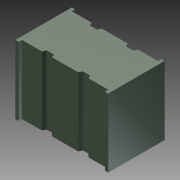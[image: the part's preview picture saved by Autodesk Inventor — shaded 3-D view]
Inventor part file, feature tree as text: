
AUTODESK INVENTOR PART (.ipt)
format: ipt  version: 2011 SP1 (Build 150282100, 282)  size: 145,920 bytes
history: native  units: in
note: dims shown in document units (in); Inventor stores cm internally (conversion verified against a paired STEP export)
features: other x21, extrude x5, sketch x5
ambient origin geometry x8: Origin, YZ Plane, XZ Plane, XY Plane, X Axis, Y Axis, Z Axis, Center Point
bodies: Solid1 (feature_tree)
feature tree (31):
  extrude  "Extrusion1"  Depth=1.0in TaperAngle=0.0deg
  extrude  "Extrusion2"  Depth=1.0in TaperAngle=0.0deg
  extrude  "Extrusion3"  [1 undecoded]
  extrude  "Extrusion4"  [1 undecoded]
  extrude  "Extrusion5"  [1 undecoded]
  other  "rot_XY"
  other  "rot_YZ"
  other  "rot_ZX"
  other  "rot_X"
  other  "rot_Y"
  other  "rot_Z"
  other  "rot_Center"
  other  "to_cover_XY"
  other  "to_cover_YZ"
  other  "to_cover_ZX"
  other  "to_cover_X"
  other  "to_cover_Y"
  other  "to_cover_Z"
  other  "to_cover_Center"
  other  "to_terminals_XY"
  other  "to_terminals_YZ"
  other  "to_terminals_ZX"
  other  "to_terminals_X"
  other  "to_terminals_Y"
  other  "to_terminals_Z"
  other  "to_terminals_Center"
  sketch  "Sketch_2"  dims[d0=0.3877in d1=0.0in d2=1.0in d3=0.0in]
  sketch  "Sketch_8"  dims[d8=0.01in d9=0.0in]
  sketch  "Sketch_5"  dims[d4=1.0in d5=0.0in d6=1.0in d7=0.0in]
  sketch  "Sketch_9"
  sketch  "Sketch_19"
note: 3 required parameter values undecoded (feature->parameter linkage not recoverable at this tier; creation-order binding heuristic only, values carry confidence <= 0.55)
